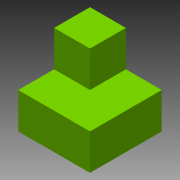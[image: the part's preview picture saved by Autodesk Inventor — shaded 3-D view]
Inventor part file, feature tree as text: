
AUTODESK INVENTOR PART (.ipt)
format: ipt  version: 2015 (Build 190159000, 159)  size: 95,232 bytes
history: native  units: in
note: dims shown in document units (in); Inventor stores cm internally (conversion verified against a paired STEP export)
features: extrude x2, sketch x2
ambient origin geometry x8: Origin, YZ Plane, XZ Plane, XY Plane, X Axis, Y Axis, Z Axis, Center Point
bodies: Solid1 (feature_tree)
feature tree (4):
  extrude  "Extrusion1"  Depth=0.75in
  extrude  "Extrusion2"  Depth=0.75in
  sketch  "Sketch1"  dims[d0=1.5in d1=0.75in]
  sketch  "Sketch2"  dims[d2=0.75in d3=0.75in d4=0.75in d5=0.0in d6=0.75in d7=0.0in]
